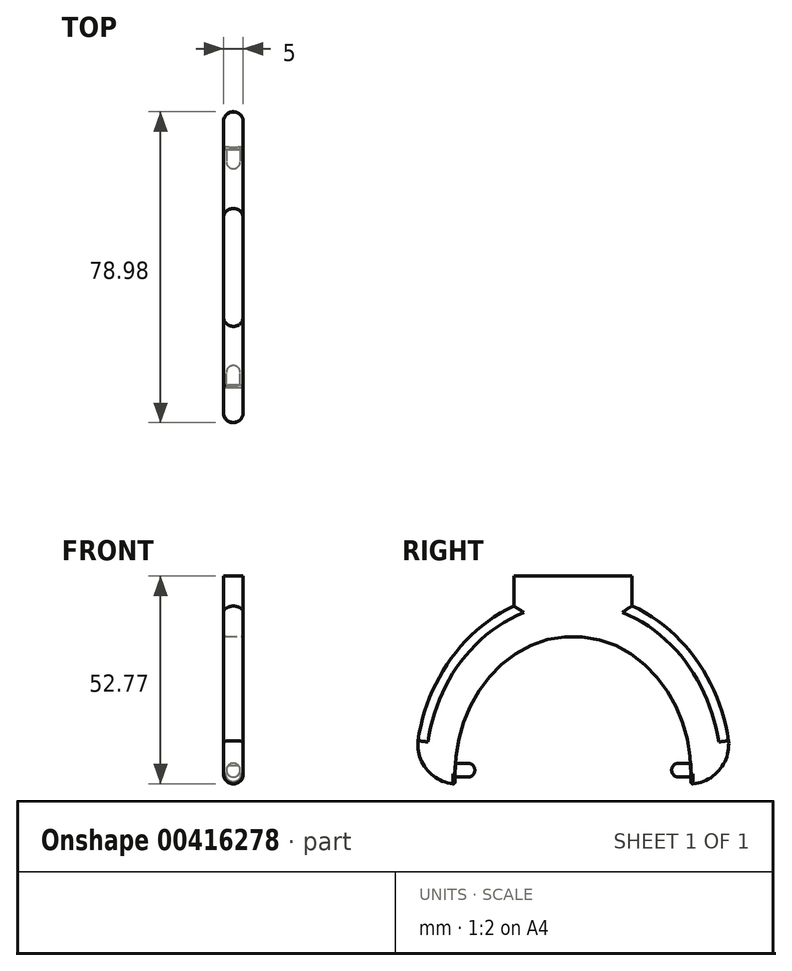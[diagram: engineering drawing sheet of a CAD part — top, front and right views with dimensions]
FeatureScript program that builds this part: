
annotation { "Feature Type Name" : "Feature", "Feature Type Description" : "" }
export const myFeature = defineFeature(function(context is Context, id is Id, definition is map)
    precondition{}
    {
        {
            var Q0;
            Q0=qCreatedBy(makeId("Right.planeOp"),FACE);
            var sketch = newSketch(context, id + "F0", { "sketchPlane" : qUnion([Q0])});
            skEllipse(sketch, "E0", {"center": v(-0.05, -1) * mm, "majorRadius": 35 * mm, "minorRadius": 30 * mm, "majorAxis": v(0, -1)});
            skEllipse(sketch, "E1", {"center": v(0, 0) * mm, "majorRadius": 45 * mm, "minorRadius": 40 * mm, "majorAxis": v(0, -1)});
            skLineSegment(sketch, "E2", {"start": v(29.95, -1) * mm, "end": v(29.87, -3.5) * mm});
            skLineSegment(sketch, "E3", {"start": v(-30.05, -1) * mm, "end": v(-29.97, -3.5) * mm});
            skLineSegment(sketch, "E4.bottom", {"start": v(-15.06, 29.3) * mm, "end": v(14.94, 29.3) * mm});
            skLineSegment(sketch, "E4.top", {"start": v(-15.06, 49.3) * mm, "end": v(14.94, 49.3) * mm});
            skLineSegment(sketch, "E4.left", {"start": v(-15.06, 29.3) * mm, "end": v(-15.06, 49.3) * mm});
            skLineSegment(sketch, "E4.right", {"start": v(14.94, 29.3) * mm, "end": v(14.94, 49.3) * mm});
            skArc(sketch, "E5", {"start": v(-39.44, 7.48) * mm, "mid": v(-37.07, -0.04) * mm, "end": v(-29.97, -3.5) * mm});
            skArc(sketch, "E6", {"start": v(29.87, -3.5) * mm, "mid": v(37.03, -0.08) * mm, "end": v(39.44, 7.48) * mm});
            skSolve(sketch);
        }
        {
            var Q0;
            {var subQ5=sQuery(id+"F0.wireOp",EDGE,"E4.top");Q0=makeQuery(id+"F0.imprint","IMPRINT",FACE,{"disambiguationData":[TD([[makeQuery(id+"F0.imprint","IMPRINT",EDGE,{"derivedFrom":subQ5}),-1.0]])]});}
            var Q1;
            {var subQ3=sQuery(id+"F0.wireOp",EDGE,"E4.right");var subQ5=sQuery(id+"F0.wireOp",EDGE,"E1");var subQ6=makeQuery(id+"F0.imprint","INTERSECT",VERTEX,{"derivedFrom":[subQ5,subQ3]});Q1=makeQuery(id+"F0.imprint","IMPRINT",FACE,{"disambiguationData":[TD([[makeQuery(id+"F0.imprint","IMPRINT",EDGE,{"disambiguationData":[TD([[subQ6,-1.0]])],"derivedFrom":subQ5}),1.0]])]});}
            var Q2;
            {var subQ1=sQuery(id+"F0.wireOp",EDGE,"E0");var subQ5=sQuery(id+"F0.wireOp",EDGE,"E3");var subQ6=makeQuery(id+"F0.imprint","INTERSECT",VERTEX,{"derivedFrom":[subQ1,subQ5]});Q2=makeQuery(id+"F0.imprint","IMPRINT",FACE,{"disambiguationData":[TD([[makeQuery(id+"F0.imprint","IMPRINT",EDGE,{"disambiguationData":[TD([[subQ6,1.0]])],"derivedFrom":subQ1}),-1.0]])]});}
            var Q3;
            {var subQ5=sQuery(id+"F0.wireOp",EDGE,"E6");Q3=makeQuery(id+"F0.imprint","IMPRINT",FACE,{"disambiguationData":[TD([[makeQuery(id+"F0.imprint","IMPRINT",EDGE,{"derivedFrom":subQ5}),1.0]])]});}
            extrude(context, id + "F1", {"entities" : qUnion([Q0, Q1, Q2, Q3]), "depth" : 5 * mm, "offsetDistance" : 25 * mm, "symmetric" : true});
        }
        {
            var Q0;
            Q0=qCreatedBy(makeId("Front.planeOp"),FACE);
            var sketch = newSketch(context, id + "F2", { "sketchPlane" : qUnion([Q0])});
            skCircle(sketch, "E7", {"center": v(0, 0) * mm, "radius": 1.75 * mm});
            skSolve(sketch);
        }
        {
            var Q0;
            Q0=makeQuery(id+"F2.imprint","IMPRINT",FACE,{"disambiguationData":[TD([[makeQuery(id+"F2.imprint","IMPRINT",EDGE,{"derivedFrom":sQuery(id+"F2.wireOp",EDGE,"E7")}),1.0]])]});
            extrude(context, id + "F3", {"entities" : qUnion([Q0]), "operationType" : NewBodyOperationType.ADD, "depth" : 30 * mm, "offsetDistance" : 25 * mm, "hasSecondDirection" : true, "secondDirectionOppositeDirection" : false, "secondDirectionDepth" : 25 * mm});
        }
        {
            var Q0;
            Q0=makeQuery(id+"F2.imprint","IMPRINT",FACE,{"disambiguationData":[TD([[makeQuery(id+"F2.imprint","IMPRINT",EDGE,{"derivedFrom":sQuery(id+"F2.wireOp",EDGE,"E7")}),1.0]])]});
            extrude(context, id + "F4", {"entities" : qUnion([Q0]), "operationType" : NewBodyOperationType.ADD, "oppositeDirection" : true, "depth" : 30 * mm, "offsetDistance" : 25 * mm, "hasSecondDirection" : true, "secondDirectionOppositeDirection" : true, "secondDirectionDepth" : 25 * mm});
        }
        {
            var Q0;
            {var subQ0=sQuery(id+"F0.wireOp",EDGE,"E1");Q0=makeQuery(id+"F1.opExtrude","CAP_EDGE",EDGE,{"disambiguationData":[OSD([subQ0]),TDD([makeQuery(id+"F0.imprint","IMPRINT",EDGE,{"disambiguationData":[TD([[makeQuery(id+"F0.imprint","INTERSECT",VERTEX,{"derivedFrom":[subQ0,sQuery(id+"F0.wireOp",EDGE,"E5")]}),1.0]])],"derivedFrom":subQ0})])],"isStart":false});}
            var Q1;
            Q1=makeQuery(id+"F1.opExtrude","CAP_EDGE",EDGE,{"disambiguationData":[OSD([sQuery(id+"F0.wireOp",EDGE,"E4.left")])],"isStart":false});
            var Q2;
            Q2=makeQuery(id+"F1.opExtrude","CAP_EDGE",EDGE,{"disambiguationData":[OSD([sQuery(id+"F0.wireOp",EDGE,"E4.right")])],"isStart":false});
            var Q3;
            Q3=makeQuery(id+"F1.opExtrude","CAP_EDGE",EDGE,{"disambiguationData":[OSD([sQuery(id+"F0.wireOp",EDGE,"E5")])],"isStart":false});
            var Q4;
            {var subQ0=sQuery(id+"F0.wireOp",EDGE,"E1");Q4=makeQuery(id+"F1.opExtrude","CAP_EDGE",EDGE,{"disambiguationData":[OSD([subQ0]),TDD([makeQuery(id+"F0.imprint","IMPRINT",EDGE,{"disambiguationData":[TD([[makeQuery(id+"F0.imprint","INTERSECT",VERTEX,{"derivedFrom":[subQ0,sQuery(id+"F0.wireOp",EDGE,"E6")]}),-1.0]])],"derivedFrom":subQ0})])],"isStart":false});}
            var Q5;
            Q5=makeQuery(id+"F1.opExtrude","CAP_EDGE",EDGE,{"disambiguationData":[OSD([sQuery(id+"F0.wireOp",EDGE,"E6")])],"isStart":false});
            var Q6;
            Q6=makeQuery(id+"F1.opExtrude","CAP_EDGE",EDGE,{"disambiguationData":[OSD([sQuery(id+"F0.wireOp",EDGE,"E6")])],"isStart":true});
            var Q7;
            {var subQ0=sQuery(id+"F0.wireOp",EDGE,"E1");Q7=makeQuery(id+"F1.opExtrude","CAP_EDGE",EDGE,{"disambiguationData":[OSD([subQ0]),TDD([makeQuery(id+"F0.imprint","IMPRINT",EDGE,{"disambiguationData":[TD([[makeQuery(id+"F0.imprint","INTERSECT",VERTEX,{"derivedFrom":[subQ0,sQuery(id+"F0.wireOp",EDGE,"E6")]}),-1.0]])],"derivedFrom":subQ0})])],"isStart":true});}
            var Q8;
            Q8=makeQuery(id+"F1.opExtrude","CAP_EDGE",EDGE,{"disambiguationData":[OSD([sQuery(id+"F0.wireOp",EDGE,"E4.right")])],"isStart":true});
            var Q9;
            Q9=makeQuery(id+"F1.opExtrude","CAP_EDGE",EDGE,{"disambiguationData":[OSD([sQuery(id+"F0.wireOp",EDGE,"E5")])],"isStart":true});
            var Q10;
            {var subQ0=sQuery(id+"F0.wireOp",EDGE,"E1");Q10=makeQuery(id+"F1.opExtrude","CAP_EDGE",EDGE,{"disambiguationData":[OSD([subQ0]),TDD([makeQuery(id+"F0.imprint","IMPRINT",EDGE,{"disambiguationData":[TD([[makeQuery(id+"F0.imprint","INTERSECT",VERTEX,{"derivedFrom":[subQ0,sQuery(id+"F0.wireOp",EDGE,"E5")]}),1.0]])],"derivedFrom":subQ0})])],"isStart":true});}
            var Q11;
            Q11=makeQuery(id+"F1.opExtrude","CAP_EDGE",EDGE,{"disambiguationData":[OSD([sQuery(id+"F0.wireOp",EDGE,"E4.left")])],"isStart":true});
            fillet(context, id + "F5", {"entities" : qUnion([Q0, Q1, Q2, Q3, Q4, Q5, Q6, Q7, Q8, Q9, Q10, Q11]), "radius" : 2.5 * mm, "tangentPropagation" : true, "allowEdgeOverflow" : false});
        }
        {
            var Q0;
            Q0=makeQuery(id+"F4.opExtrude","CAP_EDGE",EDGE,{"disambiguationData":[OSD([sQuery(id+"F2.wireOp",EDGE,"E7")])],"isStart":true});
            var Q1;
            Q1=makeQuery(id+"F3.opExtrude","CAP_EDGE",EDGE,{"disambiguationData":[OSD([sQuery(id+"F2.wireOp",EDGE,"E7")])],"isStart":true});
            fillet(context, id + "F6", {"entities" : qUnion([Q0, Q1]), "radius" : 1.75 * mm, "tangentPropagation" : true, "allowEdgeOverflow" : false});
        }
        {
            var Q0;
            Q0=makeQuery(id+"F1.opExtrude","CAP_EDGE",EDGE,{"disambiguationData":[OSD([sQuery(id+"F0.wireOp",EDGE,"E0")])],"isStart":true});
            var Q1;
            Q1=makeQuery(id+"F1.opExtrude","CAP_EDGE",EDGE,{"disambiguationData":[OSD([sQuery(id+"F0.wireOp",EDGE,"E0")])],"isStart":false});
            var Q2;
            Q2=makeQuery(id+"F5.opFillet","BLEND_EDGE",EDGE,{"blendedFrom":[makeQuery(id+"F1.opExtrude","CAP_EDGE",EDGE,{"disambiguationData":[OSD([sQuery(id+"F0.wireOp",EDGE,"E6")])],"isStart":true}),makeQuery(id+"F1.opExtrude","SWEPT_FACE",FACE,{"disambiguationData":[OSD([sQuery(id+"F0.wireOp",EDGE,"E0")])]})],"blendedInto":[makeQuery(id+"F1.opExtrude","SWEPT_FACE",FACE,{"disambiguationData":[OSD([sQuery(id+"F0.wireOp",EDGE,"E0")])]})]});
            var Q3;
            Q3=makeQuery(id+"F5.opFillet","BLEND_EDGE",EDGE,{"blendedFrom":[makeQuery(id+"F1.opExtrude","CAP_EDGE",EDGE,{"disambiguationData":[OSD([sQuery(id+"F0.wireOp",EDGE,"E6")])],"isStart":false}),makeQuery(id+"F1.opExtrude","SWEPT_FACE",FACE,{"disambiguationData":[OSD([sQuery(id+"F0.wireOp",EDGE,"E0")])]})],"blendedInto":[makeQuery(id+"F1.opExtrude","SWEPT_FACE",FACE,{"disambiguationData":[OSD([sQuery(id+"F0.wireOp",EDGE,"E0")])]})]});
            var Q4;
            Q4=makeQuery(id+"F5.opFillet","BLEND_EDGE",EDGE,{"blendedFrom":[makeQuery(id+"F1.opExtrude","CAP_EDGE",EDGE,{"disambiguationData":[OSD([sQuery(id+"F0.wireOp",EDGE,"E5")])],"isStart":true}),makeQuery(id+"F1.opExtrude","SWEPT_FACE",FACE,{"disambiguationData":[OSD([sQuery(id+"F0.wireOp",EDGE,"E0")])]})],"blendedInto":[makeQuery(id+"F1.opExtrude","SWEPT_FACE",FACE,{"disambiguationData":[OSD([sQuery(id+"F0.wireOp",EDGE,"E0")])]})]});
            var Q5;
            Q5=makeQuery(id+"F5.opFillet","BLEND_EDGE",EDGE,{"blendedFrom":[makeQuery(id+"F1.opExtrude","CAP_EDGE",EDGE,{"disambiguationData":[OSD([sQuery(id+"F0.wireOp",EDGE,"E5")])],"isStart":false}),makeQuery(id+"F1.opExtrude","SWEPT_FACE",FACE,{"disambiguationData":[OSD([sQuery(id+"F0.wireOp",EDGE,"E0")])]})],"blendedInto":[makeQuery(id+"F1.opExtrude","SWEPT_FACE",FACE,{"disambiguationData":[OSD([sQuery(id+"F0.wireOp",EDGE,"E0")])]})]});
            fillet(context, id + "F7", {"entities" : qUnion([Q0, Q1, Q2, Q3, Q4, Q5]), "radius" : .5 * mm, "tangentPropagation" : true, "allowEdgeOverflow" : false});
        }
    });
